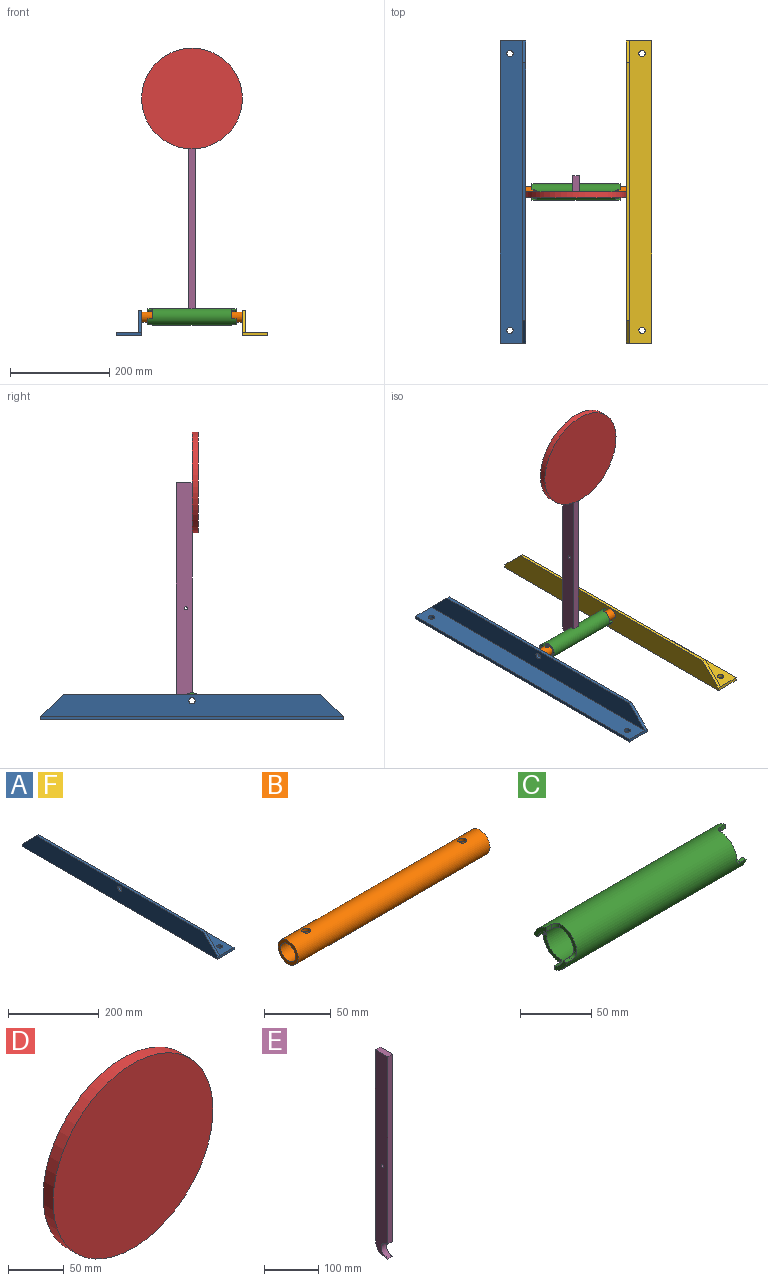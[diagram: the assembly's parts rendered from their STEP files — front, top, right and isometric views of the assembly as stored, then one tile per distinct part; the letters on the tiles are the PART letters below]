
ASSEMBLY  parts=6 mates=5
PART A: 13 faces, bbox 50.8x609.6x50.8 mm
  f0: plane 609.6x44.45mm, normal (1,0,0), area 24994.2mm2, adj f1,f5,f8,f9,f10
  f1: plane 520.7x6.35mm, normal (0,0,1), area 3306.4mm2, adj f0,f2,f9,f10
  f2: plane 609.6x50.8mm, normal (-1,0,0), area 28865.2mm2, adj f1,f3,f6,f7,f8,f9,f10
  f3: plane 609.6x50.8mm, normal (0,0,-1), area 30714.3mm2, adj f2,f4,f6,f7,f11,f12
  f4: plane 609.6x6.35mm, normal (1,0,0), area 3871mm2, adj f3,f5,f6,f7
  f5: plane 609.6x44.45mm, normal (0,0,1), area 26843.4mm2, adj f0,f4,f6,f7,f11,f12
  f6: plane 50.8x6.35mm, normal (0,-1,0), area 322.6mm2, adj f2,f3,f4,f5,f10
  f7: plane 50.8x6.35mm, normal (0,1,0), area 322.6mm2, adj f2,f3,f4,f5,f9
  f8: cylinder r=6.35mm len=12.7mm, axis (-1,0,0), area 253.4mm2, adj f0,f2
  f9: plane 44.45x44.45mm, normal (0,0.71,0.71), area 399.2mm2, adj f0,f1,f2,f7
  f10: plane 44.45x44.45mm, normal (0,-0.71,0.71), area 399.2mm2, adj f0,f1,f2,f6
  f11: cylinder r=6.35mm len=12.7mm, axis (0,0,1), area 253.4mm2, adj f3,f5
  f12: cylinder r=6.35mm len=12.7mm, axis (0,0,1), area 253.4mm2, adj f3,f5
PART B: 8 faces, bbox 203.2x21.3x21.3 mm
  f0: cylinder r=7.87mm len=203.2mm, axis (-1,0,0), area 9923.6mm2, adj f2,f3,f4,f5,f6,f7
  f1: cylinder r=10.67mm len=203.2mm, axis (-1,0,0), area 13492.2mm2, adj f2,f3,f4,f5,f6,f7
  f2: plane 21.34x21.34mm, normal (1,0,0), area 162.8mm2, adj f0,f1
  f3: plane 21.34x21.34mm, normal (-1,0,0), area 162.8mm2, adj f0,f1
  f4: cylinder r=3.17mm len=6.35mm, axis (0,0,1), area 57.5mm2, adj f0,f1
  f5: cylinder r=3.17mm len=6.35mm, axis (0,0,1), area 57.6mm2, adj f0,f1
  f6: cylinder r=3.17mm len=6.35mm, axis (0,0,1), area 57.5mm2, adj f0,f1
  f7: cylinder r=3.17mm len=6.35mm, axis (0,0,1), area 57.6mm2, adj f0,f1
PART C: 26 faces, bbox 177.8x33.4x33.4 mm
  f0: cylinder r=13.33mm len=177.8mm, axis (-1,0,0), area 13820.4mm2, adj f2,f3,f4,f5,f6,f7,f8,f9
  f1: cylinder r=16.7mm len=177.8mm, axis (-1,0,0), area 17380.2mm2, adj f2,f3,f4,f5,f6,f7,f8,f9
  f2: plane 12.26x12.26mm, normal (-1,0,0), area 52.4mm2, adj f0,f1,f14,f17
  f3: plane 12.26x12.26mm, normal (-1,0,0), area 52.4mm2, adj f0,f1,f13,f16
  f4: plane 12.26x12.26mm, normal (1,0,0), area 52.4mm2, adj f0,f1,f8,f10
  f5: plane 12.26x12.26mm, normal (1,0,0), area 52.4mm2, adj f0,f1,f7,f11
  f6: plane 16.69x16.69mm, normal (1,0,0), area 79.3mm2, adj f0,f1,f24,f25
  f7: plane 5.56x3.49mm, normal (0,0,-1), area 19.4mm2, adj f0,f1,f5,f24
  f8: plane 5.56x3.49mm, normal (0,1,0), area 19.4mm2, adj f0,f1,f4,f25
  f9: plane 16.69x16.69mm, normal (1,0,0), area 79.3mm2, adj f0,f1,f22,f23
  f10: plane 5.56x3.49mm, normal (0,0,1), area 19.4mm2, adj f0,f1,f4,f22
  f11: plane 5.56x3.49mm, normal (0,-1,0), area 19.4mm2, adj f0,f1,f5,f23
  f12: plane 16.69x16.69mm, normal (-1,0,0), area 79.3mm2, adj f0,f1,f20,f21
  f13: plane 5.56x3.49mm, normal (0,0,1), area 19.4mm2, adj f0,f1,f3,f21
  f14: plane 5.56x3.49mm, normal (0,-1,0), area 19.4mm2, adj f0,f1,f2,f20
  f15: plane 16.69x16.69mm, normal (-1,0,0), area 79.3mm2, adj f0,f1,f18,f19
  f16: plane 5.56x3.49mm, normal (0,1,0), area 19.4mm2, adj f0,f1,f3,f18
  f17: plane 5.56x3.49mm, normal (0,0,-1), area 19.4mm2, adj f0,f1,f2,f19
  f18: cylinder r=3.97mm len=3.97mm, axis (0,0,1), area 21.4mm2, adj f0,f1,f15,f16
  f19: cylinder r=3.97mm len=3.97mm, axis (0,1,0), area 21.4mm2, adj f0,f1,f15,f17
  f20: cylinder r=3.97mm len=3.97mm, axis (0,0,-1), area 21.4mm2, adj f0,f1,f12,f14
  f21: cylinder r=3.97mm len=3.97mm, axis (0,-1,0), area 21.4mm2, adj f0,f1,f12,f13
  f22: cylinder r=3.97mm len=3.97mm, axis (0,1,0), area 21.4mm2, adj f0,f1,f9,f10
  f23: cylinder r=3.97mm len=3.97mm, axis (0,0,1), area 21.4mm2, adj f0,f1,f9,f11
  f24: cylinder r=3.97mm len=3.97mm, axis (0,-1,0), area 21.4mm2, adj f0,f1,f6,f7
  f25: cylinder r=3.97mm len=3.97mm, axis (0,0,-1), area 21.4mm2, adj f0,f1,f6,f8
PART D: 3 faces, bbox 203.2x12.7x203.2 mm
  f0: cylinder r=101.6mm len=203.2mm, axis (0,1,0), area 8107.3mm2, adj f1,f2
  f1: plane 203.2x203.2mm, normal (0,-1,0), area 32429.3mm2, adj f0
  f2: plane 203.2x203.2mm, normal (0,1,0), area 32429.3mm2, adj f0
PART E: 9 faces, bbox 12.7x31.8x457.2 mm
  f0: plane 423.8x12.7mm, normal (0,-1,0), area 5382.2mm2, adj f1,f5,f6,f7
  f1: cylinder r=16.7mm len=33.4mm, axis (-1,0,0), area 666.3mm2, adj f0,f2,f6,f7
  f2: plane 12.7x6.35mm, normal (0,0,-1), area 80.6mm2, adj f1,f3,f6,f7
  f3: cylinder r=25.4mm len=25.4mm, axis (-1,0,0), area 506.7mm2, adj f2,f4,f6,f7
  f4: plane 431.8x12.7mm, normal (0,1,0), area 5483.9mm2, adj f3,f5,f6,f7
  f5: plane 31.75x12.7mm, normal (0,0,1), area 403.2mm2, adj f0,f4,f6,f7
  f6: plane 457.2x31.75mm, normal (1,0,0), area 13907.9mm2, adj f0,f1,f2,f3,f4,f5,f8
  f7: plane 457.2x31.75mm, normal (-1,0,0), area 13907.9mm2, adj f0,f1,f2,f3,f4,f5,f8
  f8: cylinder r=3.17mm len=12.7mm, axis (1,0,0), area 253.4mm2, adj f6,f7
PART F: same geometry as A
PLACE A rot(axis=(0,0,1),180deg) t=(-203.2,0,0)mm
PLACE B t=(-101.6,0,38.1)mm
PLACE C t=(-101.6,0,38.1)mm
PLACE D t=(-101.6,0,478.6)mm
PLACE E t=(-101.6,0,38.1)mm
PLACE F at identity fixed
MATE fastened B.f1 <-> F.f8  axis (1,0,0) through (0,0,38.1)mm
MATE fastened A.f8 <-> B.f1  axis (1,0,0) through (-203.2,0,38.1)mm
MATE fastened D.f0 <-> E.f0  axis (0,1,0) through (-101.6,0,478.6)mm
MATE fastened C.f1 <-> E.f1  axis (-1,0,0) through (-101.6,0,38.1)mm
MATE revolute B.f1 <-> C.f1  axis (1,0,0) through (0,0,38.1)mm
